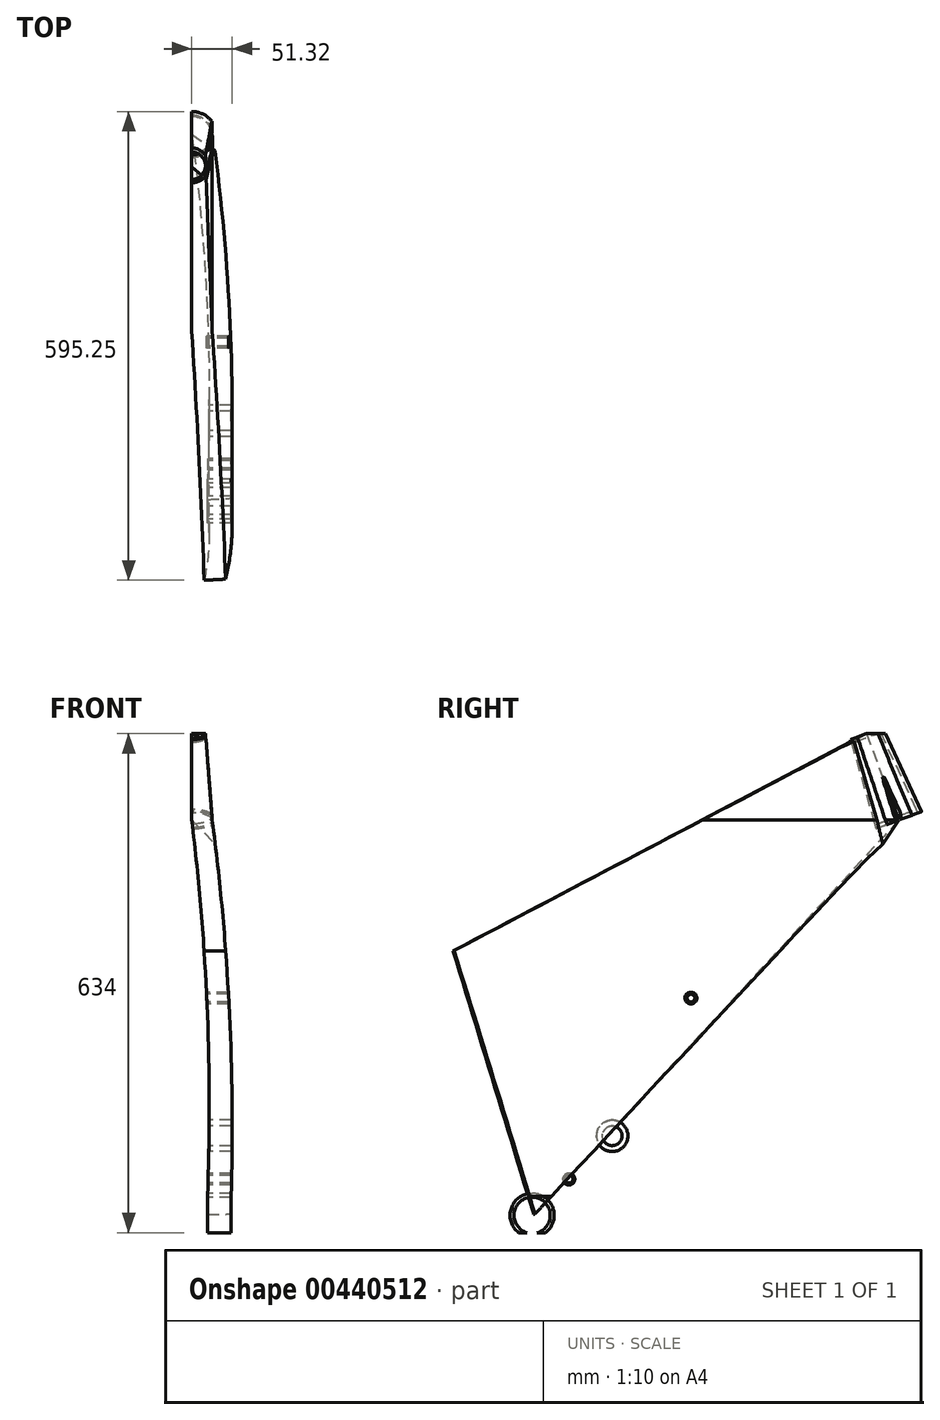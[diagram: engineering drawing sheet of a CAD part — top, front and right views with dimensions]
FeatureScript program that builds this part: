
annotation { "Feature Type Name" : "Feature", "Feature Type Description" : "" }
export const myFeature = defineFeature(function(context is Context, id is Id, definition is map)
    precondition{}
    {
        {
            var Q0;
            Q0=qCreatedBy(makeId("Right.planeOp"),FACE);
            var sketch = newSketch(context, id + "F0", { "sketchPlane" : qUnion([Q0])});
            skLineSegment(sketch, "E0", {"start": v(0, 0) * mm, "end": v(-83.68, 223.8) * mm, "construction": true});
            skLineSegment(sketch, "E1", {"start": v(-295.85, 645.65) * mm, "end": v(-16.13, -102.49) * mm, "construction": true});
            skPoint(sketch, "E2", {"position": v(-219.37, 441.1) * mm});
            skLineSegment(sketch, "E3", {"start": v(-285.85, 416.25) * mm, "end": v(-152.9, 465.96) * mm, "construction": true});
            skCircle(sketch, "E4", {"center": v(52.32, 5.34) * mm, "radius": 375.7 * mm, "construction": true});
            skPoint(sketch, "E5", {"position": v(-260.46, 551) * mm});
            skPoint(sketch, "E6", {"position": v(-683.46, -60) * mm});
            skPoint(sketch, "E7", {"position": v(-1124.4, 0) * mm});
            skLineSegment(sketch, "E8", {"start": v(-1124.4, 0) * mm, "end": v(0, 0) * mm, "construction": true});
            skCircle(sketch, "E9", {"center": v(-1124.4, 0) * mm, "radius": 375.7 * mm, "construction": true});
            skLineSegment(sketch, "E10", {"start": v(-683.46, -60) * mm, "end": v(-904.4, 662.68) * mm, "construction": true});
            skLineSegment(sketch, "E11", {"start": v(-260.46, 551) * mm, "end": v(-947.84, 551) * mm, "construction": true});
            skPoint(sketch, "E12", {"position": v(-870.26, 551) * mm});
            skLineSegment(sketch, "E13", {"start": v(-207.61, 570.76) * mm, "end": v(-313.3, 531.24) * mm, "construction": true});
            skPoint(sketch, "E14", {"position": v(-240.15, 496.67) * mm});
            skLineSegment(sketch, "E15", {"start": v(-683.46, -60) * mm, "end": v(-240.15, 496.67) * mm, "construction": true});
            skPoint(sketch, "E16", {"position": v(-785.79, 274.7) * mm});
            skLineSegment(sketch, "E17", {"start": v(-785.79, 274.7) * mm, "end": v(-240.15, 496.67) * mm, "construction": true});
            skPoint(sketch, "E18", {"position": v(-461.8, 218.34) * mm});
            skPoint(sketch, "E19", {"position": v(-512.97, 385.69) * mm});
            skPoint(sketch, "E20", {"position": v(-583.46, 40) * mm});
            skPoint(sketch, "E21", {"position": v(-483.46, 215) * mm});
            skSolve(sketch);
        }
        {
            var Q0;
            Q0=qCreatedBy(makeId("Right.planeOp"),FACE);
            var sketch = newSketch(context, id + "F1", { "sketchPlane" : qUnion([Q0])});
            skLineSegment(sketch, "E22", {"start": v(-243.73, 432) * mm, "end": v(-245.48, 436.69) * mm});
            skLineSegment(sketch, "E23", {"start": v(-275.1, 540.19) * mm, "end": v(-245.48, 436.69) * mm});
            skLineSegment(sketch, "E24", {"start": v(-275.1, 540.19) * mm, "end": v(-276.85, 544.87) * mm});
            skLineSegment(sketch, "E25", {"start": v(-276.85, 544.87) * mm, "end": v(-280.8, 543.4) * mm});
            skLineSegment(sketch, "E26", {"start": v(-280.8, 543.4) * mm, "end": v(-248.4, 430.25) * mm});
            skLineSegment(sketch, "E27", {"start": v(-248.4, 430.25) * mm, "end": v(-243.73, 432) * mm});
            skSolve(sketch);
        }
        {
            var Q0;
            Q0=qSketchRegion(id+"F1",true);
            var Q1;
            Q1=sQuery(id+"F0.wireOp",EDGE,"E1");
            revolve(context, id + "F2", {"entities" : qUnion([Q0]), "axis" : qUnion([Q1]), "revolveType" : RevolveType.FULL});
        }
        {
            var Q0;
            Q0=qCreatedBy(makeId("Right.planeOp"),FACE);
            var sketch = newSketch(context, id + "F3", { "sketchPlane" : qUnion([Q0])});
            skCircle(sketch, "E28", {"center": v(-685.15, -60.91) * mm, "radius": 23 * mm});
            skCircle(sketch, "E29", {"center": v(-685.15, -60.91) * mm, "radius": 28 * mm});
            skSolve(sketch);
        }
        {
            var Q0;
            Q0=qSketchRegion(id+"F3",true);
            extrude(context, id + "F4", {"entities" : qUnion([Q0]), "endBound" : BoundingType.SYMMETRIC, "depth" : 100 * mm});
        }
        {
            var Q0;
            Q0=qCreatedBy(makeId("Right.planeOp"),FACE);
            var sketch = newSketch(context, id + "F5", { "sketchPlane" : qUnion([Q0])});
            skCircle(sketch, "E30", {"center": v(-583.46, 40) * mm, "radius": 20 * mm});
            skCircle(sketch, "E31", {"center": v(-583.46, 40) * mm, "radius": 12.5 * mm});
            skSolve(sketch);
        }
        {
            var Q0;
            Q0=qCreatedBy(makeId("Right.planeOp"),FACE);
            var sketch = newSketch(context, id + "F6", { "sketchPlane" : qUnion([Q0])});
            skLineSegment(sketch, "E32", {"start": v(-1125.68, 11.93) * mm, "end": v(-586.66, 69.83) * mm});
            skLineSegment(sketch, "E33", {"start": v(-582.24, 10.02) * mm, "end": v(-1123.9, -12) * mm});
            skArc(sketch, "E34", {"start": v(-582.24, 10.02) * mm, "mid": v(-553.54, 42.21) * mm, "end": v(-586.66, 69.83) * mm});
            skArc(sketch, "E35", {"start": v(-1125.68, 11.93) * mm, "mid": v(-1136.36, -0.88) * mm, "end": v(-1123.9, -12) * mm});
            skCircle(sketch, "E36", {"center": v(-583.46, 40) * mm, "radius": 21 * mm});
            skCircle(sketch, "E37", {"center": v(-1124.4, 0) * mm, "radius": 6 * mm});
            skSolve(sketch);
        }
        {
            var Q0;
            Q0 = qSketchRegion(id + "F6", true);
            extrude(context, id + "F7", {"entities" : qUnion([Q0]), "endBound" : BoundingType.SYMMETRIC, "depth" : 200 * mm});
        }
        {
            var Q0;
            Q0=makeQuery(id+"F7.opExtrude","SWEPT_FACE",FACE,{"disambiguationData":[OSD([sQuery(id+"F6.wireOp",EDGE,"E32")])]});
            var sketch = newSketch(context, id + "F8", { "sketchPlane" : qUnion([Q0])});
            skLineSegment(sketch, "E38", {"start": v(-30, -501.33) * mm, "end": v(-30, -665.96) * mm});
            skLineSegment(sketch, "E39", {"start": v(-30, -665.96) * mm, "end": v(-85, -725.96) * mm});
            skLineSegment(sketch, "E40", {"start": v(-30, -501.33) * mm, "end": v(-100, -501.33) * mm});
            skLineSegment(sketch, "E41", {"start": v(-100, -501.33) * mm, "end": v(-100, -1257.57) * mm});
            skLineSegment(sketch, "E42", {"start": v(-100, -1257.57) * mm, "end": v(-85, -1257.57) * mm});
            skLineSegment(sketch, "E43", {"start": v(-85, -725.96) * mm, "end": v(-85, -1257.57) * mm});
            skSolve(sketch);
        }
        {
            var Q0;
            Q0 = qSketchRegion(id + "F8", true);
            extrude(context, id + "F9", {"entities" : qUnion([Q0]), "operationType" : NewBodyOperationType.REMOVE, "endBound" : BoundingType.SYMMETRIC, "depth" : 400 * mm});
        }
        {
            var Q0;
            Q0=qCreatedBy(makeId("Top.planeOp"),FACE);
            var sketch = newSketch(context, id + "F10", { "sketchPlane" : qUnion([Q0])});
            skLineSegment(sketch, "E44", {"start": v(0, -513.07) * mm, "end": v(0, -673.46) * mm});
            skLineSegment(sketch, "E45", {"start": v(0, -673.46) * mm, "end": v(-65, -759.54) * mm});
            skLineSegment(sketch, "E46", {"start": v(-65, -759.54) * mm, "end": v(-75, -1191.95) * mm});
            skLineSegment(sketch, "E47", {"start": v(-75, -1191.95) * mm, "end": v(100, -1191.95) * mm});
            skLineSegment(sketch, "E48", {"start": v(100, -1191.95) * mm, "end": v(100, -513.07) * mm});
            skLineSegment(sketch, "E49", {"start": v(100, -513.07) * mm, "end": v(0, -513.07) * mm});
            skSolve(sketch);
        }
        {
            var Q0;
            Q0 = qSketchRegion(id + "F10", true);
            var Q1;
            Q1=makeQuery(id+"F7.opExtrude","SWEPT_FACE",FACE,{"disambiguationData":[OSD([sQuery(id+"F6.wireOp",EDGE,"E32")])]});
            var Q2;
            Q2=makeQuery(id+"F12.opExtrude","SWEPT_BODY",BODY,{"disambiguationData":[OSD([sQuery(id+"F5.wireOp",EDGE,"E30"),sQuery(id+"F5.wireOp",EDGE,"E31")])]});
            var Q3;
            Q3=makeQuery(id+"F7.opExtrude","SWEPT_FACE",FACE,{"disambiguationData":[OSD([sQuery(id+"F6.wireOp",EDGE,"E33")])]});
            extrude(context, id + "F11", {"entities" : qUnion([Q0]), "operationType" : NewBodyOperationType.REMOVE, "endBound" : BoundingType.UP_TO_SURFACE, "endBoundEntityFace" : qUnion([Q1]), "endBoundEntityBody" : qUnion([Q2]), "depth" : 25 * mm, "hasSecondDirection" : true, "secondDirectionBound" : SecondDirectionBoundingType.UP_TO_SURFACE, "secondDirectionOppositeDirection" : true, "secondDirectionBoundEntityFace" : qUnion([Q3]), "secondDirectionDepth" : 25 * mm});
        }
        {
            var Q0;
            Q0 = qSketchRegion(id + "F5", true);
            extrude(context, id + "F12", {"entities" : qUnion([Q0]), "endBound" : BoundingType.SYMMETRIC, "depth" : 100 * mm});
        }
        {
            var Q0;
            Q0=qCreatedBy(makeId("Right.planeOp"),FACE);
            var sketch = newSketch(context, id + "F13", { "sketchPlane" : qUnion([Q0])});
            skCircle(sketch, "E50", {"center": v(-638.46, -15) * mm, "radius": 7.5 * mm});
            skCircle(sketch, "E51", {"center": v(-638.46, -15) * mm, "radius": 5 * mm});
            skSolve(sketch);
        }
        {
            var Q0;
            Q0 = qSketchRegion(id + "F13", true);
            extrude(context, id + "F14", {"entities" : qUnion([Q0]), "endBound" : BoundingType.SYMMETRIC, "depth" : 100 * mm});
        }
        {
            var Q0;
            Q0=makeQuery(id+"F11.boolean.opBoolean","COPY",EDGE,{"derivedFrom":makeQuery(id+"F11.opExtrude","TWEAK_EDGE",EDGE,{"derivedFrom":[makeQuery(id+"F10.imprint","IMPRINT",EDGE,{"derivedFrom":sQuery(id+"F10.wireOp",EDGE,"E45")}),makeQuery(id+"F10.imprint","IMPRINT",EDGE,{"derivedFrom":sQuery(id+"F10.wireOp",EDGE,"E46")})]})});
            var Q1;
            Q1=makeQuery(id+"F11.boolean.opBoolean","COPY",EDGE,{"derivedFrom":makeQuery(id+"F11.opExtrude","TWEAK_EDGE",EDGE,{"derivedFrom":[makeQuery(id+"F10.imprint","IMPRINT",EDGE,{"derivedFrom":sQuery(id+"F10.wireOp",EDGE,"E44")}),makeQuery(id+"F10.imprint","IMPRINT",EDGE,{"derivedFrom":sQuery(id+"F10.wireOp",EDGE,"E45")})]})});
            var Q2;
            Q2=makeQuery(id+"F9.boolean.opBoolean","COPY",EDGE,{"derivedFrom":makeQuery(id+"F9.opExtrude","SWEPT_EDGE",EDGE,{"disambiguationData":[OSD([sQuery(id+"F8.wireOp",EDGE,"E39"),sQuery(id+"F8.wireOp",EDGE,"E43")])]})});
            var Q3;
            Q3=makeQuery(id+"F9.boolean.opBoolean","COPY",EDGE,{"derivedFrom":makeQuery(id+"F9.opExtrude","SWEPT_EDGE",EDGE,{"disambiguationData":[OSD([sQuery(id+"F8.wireOp",EDGE,"E38"),sQuery(id+"F8.wireOp",EDGE,"E39")])]})});
            fillet(context, id + "F15", {"entities" : qUnion([Q0, Q1, Q2, Q3]), "radius" : 50 * mm, "tangentPropagation" : true, "allowEdgeOverflow" : false});
        }
        {
            var Q0;
            Q0=makeQuery(id+"F11.boolean.opBoolean","COPY",EDGE,{"derivedFrom":makeQuery(id+"F11.opExtrude","CAP_EDGE",EDGE,{"disambiguationData":[OSD([sQuery(id+"F10.wireOp",EDGE,"E46")]),topologyDisambiguationEdgeConnected([makeQuery(id+"F7.opExtrude","SWEPT_FACE",FACE,{"disambiguationData":[OSD([sQuery(id+"F6.wireOp",EDGE,"E32")])]})])],"isStart":false})});
            var Q1;
            Q1=makeQuery(id+"F9.boolean.opBoolean","INTERSECT",EDGE,{"derivedFrom":[makeQuery(id+"F7.opExtrude","SWEPT_FACE",FACE,{"disambiguationData":[OSD([sQuery(id+"F6.wireOp",EDGE,"E33")])]}),makeQuery(id+"F9.opExtrude","SWEPT_FACE",FACE,{"disambiguationData":[OSD([sQuery(id+"F8.wireOp",EDGE,"E43")])]})]});
            var Q2;
            Q2=makeQuery(id+"F9.boolean.opBoolean","INTERSECT",EDGE,{"derivedFrom":[makeQuery(id+"F7.opExtrude","SWEPT_FACE",FACE,{"disambiguationData":[OSD([sQuery(id+"F6.wireOp",EDGE,"E35")])]}),makeQuery(id+"F9.opExtrude","SWEPT_FACE",FACE,{"disambiguationData":[OSD([sQuery(id+"F8.wireOp",EDGE,"E43")])]})]});
            fillet(context, id + "F16", {"entities" : qUnion([Q0, Q1, Q2]), "radius" : 5 * mm, "tangentPropagation" : true, "allowEdgeOverflow" : false});
        }
        {
            var Q0;
            Q0=qCreatedBy(makeId("Right.planeOp"),FACE);
            var sketch = newSketch(context, id + "F17", { "sketchPlane" : qUnion([Q0])});
            skCircle(sketch, "E52", {"center": v(-723.46, 69.7) * mm, "radius": 2.5 * mm});
            skCircle(sketch, "E53", {"center": v(-665.95, -27) * mm, "radius": 2.5 * mm});
            skCircle(sketch, "E54", {"center": v(-638.46, -15) * mm, "radius": 5 * mm});
            skLineSegment(sketch, "E55", {"start": v(-664.3, -32.77) * mm, "end": v(-635.72, -24.62) * mm});
            skLineSegment(sketch, "E56", {"start": v(-719.37, 74.1) * mm, "end": v(-631.64, -7.69) * mm});
            skArc(sketch, "E57", {"start": v(-719.37, 74.1) * mm, "mid": v(-728.26, 73.3) * mm, "end": v(-726.54, 64.55) * mm});
            skArc(sketch, "E58", {"start": v(-671.95, -27.24) * mm, "mid": v(-669.47, -31.86) * mm, "end": v(-664.3, -32.77) * mm});
            skArc(sketch, "E59", {"start": v(-635.72, -24.62) * mm, "mid": v(-628.74, -17.34) * mm, "end": v(-631.64, -7.69) * mm});
            skArc(sketch, "E60", {"start": v(-671.95, -27.24) * mm, "mid": v(-687.62, 25.57) * mm, "end": v(-726.54, 64.55) * mm});
            skSolve(sketch);
        }
        {
            var Q0;
            Q0 = qSketchRegion(id + "F17", true);
            extrude(context, id + "F18", {"entities" : qUnion([Q0]), "depth" : 10 * mm});
        }
        {
            var Q0;
            Q0=qCreatedBy(makeId("Right.planeOp"),FACE);
            var sketch = newSketch(context, id + "F19", { "sketchPlane" : qUnion([Q0])});
            skCircle(sketch, "E61", {"center": v(-483.46, 215) * mm, "radius": 7.5 * mm});
            skCircle(sketch, "E62", {"center": v(-483.46, 215) * mm, "radius": 5 * mm});
            skSolve(sketch);
        }
        {
            var Q0;
            Q0 = qSketchRegion(id + "F19", true);
            extrude(context, id + "F20", {"entities" : qUnion([Q0]), "endBound" : BoundingType.SYMMETRIC, "depth" : 100 * mm});
        }
        {
            var Q0;
            Q0=qCreatedBy(makeId("Right.planeOp"),FACE);
            var sketch = newSketch(context, id + "F21", { "sketchPlane" : qUnion([Q0])});
            skLineSegment(sketch, "E63", {"start": v(-260.46, 551) * mm, "end": v(-785.79, 274.7) * mm});
            skLineSegment(sketch, "E64", {"start": v(-260.46, 551) * mm, "end": v(-218.69, 442) * mm});
            skLineSegment(sketch, "E65", {"start": v(-218.69, 442) * mm, "end": v(-285.85, 416.25) * mm});
            skLineSegment(sketch, "E66", {"start": v(-285.85, 416.25) * mm, "end": v(-662.9, -77.9) * mm});
            skArc(sketch, "E67", {"start": v(-688.41, -6.08) * mm, "mid": v(-712.44, 142.87) * mm, "end": v(-785.79, 274.7) * mm});
            skLineSegment(sketch, "E68", {"start": v(-736.26, 266.86) * mm, "end": v(-366.87, 461.14) * mm});
            skLineSegment(sketch, "E69", {"start": v(-339.34, 428.57) * mm, "end": v(-575.77, 118.7) * mm});
            skArc(sketch, "E70", {"start": v(-673.55, 136.4) * mm, "mid": v(-699.86, 204.05) * mm, "end": v(-736.26, 266.86) * mm});
            skArc(sketch, "E71", {"start": v(-339.34, 428.57) * mm, "mid": v(-340.02, 455.9) * mm, "end": v(-366.87, 461.14) * mm});
            skPoint(sketch, "E71.endSnap0", {"position": v(-523.12, 412.85) * mm});
            skPoint(sketch, "E72.startSnap0", {"position": v(-689.64, 33.27) * mm});
            skArc(sketch, "E73", {"start": v(-662.9, -77.9) * mm, "mid": v(-666.16, -40.34) * mm, "end": v(-703.86, -40.08) * mm});
            skArc(sketch, "E74", {"start": v(-703.86, -40.08) * mm, "mid": v(-692.58, -24.7) * mm, "end": v(-688.41, -6.08) * mm});
            skArc(sketch, "E75", {"start": v(-673.55, 136.4) * mm, "mid": v(-630.07, 97.65) * mm, "end": v(-575.77, 118.7) * mm});
            skSolve(sketch);
        }
        {
            var Q0;
            Q0=qCreatedBy(makeId("Right.planeOp"),FACE);
            var sketch = newSketch(context, id + "F22", { "sketchPlane" : qUnion([Q0])});
            skLineSegment(sketch, "E76", {"start": v(-260.46, 551) * mm, "end": v(-219.37, 441.1) * mm});
            skLineSegment(sketch, "E77", {"start": v(-219.37, 441.1) * mm, "end": v(-683.46, -60) * mm});
            skLineSegment(sketch, "E78", {"start": v(-683.46, -60) * mm, "end": v(-785.79, 274.7) * mm});
            skLineSegment(sketch, "E79", {"start": v(-785.79, 274.7) * mm, "end": v(-260.46, 551) * mm});
            skSolve(sketch);
        }
        {
            var Q0;
            Q0 = qSketchRegion(id + "F22", true);
            var Q1;
            Q1=sQuery(id+"F0.wireOp",EDGE,"E1");
            revolve(context, id + "F23", {"entities" : qUnion([Q0]), "axis" : qUnion([Q1]), "revolveType" : RevolveType.SYMMETRIC, "angle" : 90 * degree});
        }
        {
            var Q0;
            Q0=qCreatedBy(makeId("Front.planeOp"),FACE);
            var sketch = newSketch(context, id + "F24", { "sketchPlane" : qUnion([Q0])});
            skLineSegment(sketch, "E80", {"start": v(17.5, 551) * mm, "end": v(26, 441.1) * mm});
            skLineSegment(sketch, "E81", {"start": v(50, -83) * mm, "end": v(50, -37) * mm});
            skArc(sketch, "E82", {"start": v(50, -37) * mm, "mid": v(47.55, 202.53) * mm, "end": v(26, 441.1) * mm});
            skLineSegment(sketch, "E83", {"start": v(0, 551) * mm, "end": v(0, 441.1) * mm});
            skLineSegment(sketch, "E84", {"start": v(20, -83) * mm, "end": v(20, -37) * mm});
            skArc(sketch, "E85", {"start": v(20, -37) * mm, "mid": v(19.55, 202.45) * mm, "end": v(0, 441.1) * mm});
            skLineSegment(sketch, "E86", {"start": v(529.67, 551) * mm, "end": v(529.67, -91.58) * mm});
            skLineSegment(sketch, "E87", {"start": v(-559.2, 551) * mm, "end": v(-559.2, -83) * mm});
            skLineSegment(sketch, "E88", {"start": v(20, -83) * mm, "end": v(50, -83) * mm});
            skLineSegment(sketch, "E89", {"start": v(-559.2, -83) * mm, "end": v(-559.2, -228.99) * mm});
            skLineSegment(sketch, "E90", {"start": v(-559.2, -228.99) * mm, "end": v(534.6, -228.99) * mm});
            skLineSegment(sketch, "E91", {"start": v(534.6, -228.99) * mm, "end": v(529.67, -91.58) * mm});
            skLineSegment(sketch, "E92", {"start": v(529.67, 551) * mm, "end": v(529.67, 666.6) * mm});
            skLineSegment(sketch, "E93", {"start": v(529.67, 666.6) * mm, "end": v(-559.2, 666.6) * mm});
            skLineSegment(sketch, "E94", {"start": v(-559.2, 666.6) * mm, "end": v(-559.2, 551) * mm});
            skLineSegment(sketch, "E95", {"start": v(0, 551) * mm, "end": v(17.5, 551) * mm});
            skSolve(sketch);
        }
        {
            var Q0;
            Q0 = qSketchRegion(id + "F24", true);
            var Q1;
            Q1=makeQuery(id+"F23.opRevolve","SWEPT_BODY",BODY,{"disambiguationData":[OSD([sQuery(id+"F22.wireOp",EDGE,"E76"),sQuery(id+"F22.wireOp",EDGE,"E77"),sQuery(id+"F22.wireOp",EDGE,"E78"),sQuery(id+"F22.wireOp",EDGE,"E79")])]});
            var Q2;
            Q2=makeQuery(id+"F23.opRevolve","SWEPT_BODY",BODY,{"disambiguationData":[OSD([sQuery(id+"F22.wireOp",EDGE,"E76"),sQuery(id+"F22.wireOp",EDGE,"E77"),sQuery(id+"F22.wireOp",EDGE,"E78"),sQuery(id+"F22.wireOp",EDGE,"E79")])]});
            extrude(context, id + "F25", {"entities" : qUnion([Q0]), "operationType" : NewBodyOperationType.REMOVE, "endBound" : BoundingType.SYMMETRIC, "endBoundEntityBody" : qUnion([Q1]), "depth" : 3000 * mm, "hasSecondDirection" : true, "secondDirectionBound" : SecondDirectionBoundingType.UP_TO_BODY, "secondDirectionOppositeDirection" : true, "secondDirectionBoundEntityBody" : qUnion([Q2]), "secondDirectionDepth" : 25 * mm});
        }
    });
